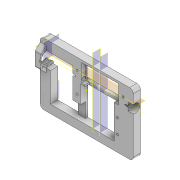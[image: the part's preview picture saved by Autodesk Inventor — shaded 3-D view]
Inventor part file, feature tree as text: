
AUTODESK INVENTOR PART (.ipt)
format: ipt  version: 2022 (Build 260153000, 153)  size: 440,832 bytes
history: native  units: mm
features: sketch x17, extrude x16, other x12, reference x8, plane x7, projected_geometry x7, fillet x3, chamfer x1, mirror x1
ambient origin geometry x8: Origin, YZ Plane, XZ Plane, XY Plane, X Axis, Y Axis, Z Axis, Center Point
bodies: Solid1 (feature_tree)
feature tree (72):
  extrude  "Extrusion1"  Depth=10.0mm
  fillet  "Fillet1"  Radius=10.0mm
  extrude  "Extrusion2"  Depth=51.0mm
  extrude  "Extrusion3"  Depth=20.0mm
  plane  "Work Plane1"
  plane  "Work Plane2"
  chamfer  "Chamfer1"  [1 undecoded]
  plane  "Work Plane3"
  extrude  "Extrusion12"  Depth=10.0mm
  extrude  "Extrusion13"  Depth=12.0mm
  mirror  "Mirror1"
  plane  "Work Plane4"
  plane  "Work Plane5"
  plane  "Arbeitsebene7"
  extrude  "Extrusion27"  Depth=7.0mm
  extrude  "Extrusion28"  Depth=0.5mm TaperAngle=0.0deg
  extrude  "Extrusion29"  Depth=0.5mm
  fillet  "Rundung6"  Radius=1.0mm
  extrude  "Extrusion37"  TaperAngle=45.0deg  [1 undecoded]
  extrude  "Extrusion38"  Depth=10.0mm
  fillet  "Rundung7"  [1 undecoded]
  extrude  "Extrusion39"  Depth=10.0mm TaperAngle=0.0deg
  other  "Arbeitsachse1"
  sketch  "Skizze44"  dims[d145=8.0mm d146=0.0mm d147=0.5mm d148=1.0mm d149=0.0mm]
  extrude  "Extrusion41"  TaperAngle=0.0deg  [1 undecoded]
  extrude  "Extrusion42"  Depth=2.0mm TaperAngle=0.0deg
  extrude  "Extrusion43"  Depth=2.5mm
  extrude  "Extrusion44"  Depth=0.5mm
  sketch  "Skizze49"  dims[d195=20.0mm d196=2.0mm d197=0.0mm d199=14.0mm d201=0.5mm d203=0.5mm d204=1.0mm d205=3.0mm d206=2.8mm d207=2.8mm d208=2.8mm d209=2.8mm d210=2.8mm d211=0.0mm d212=0.0mm d213=3.0mm d214=0.0mm d215=6.0mm d216=2.0mm d217=3.0mm d218=0.0mm d219=2.5mm d220=0.0mm]
  plane  "Arbeitsebene10"
  extrude  "Extrusion45"  Depth=0.5mm
  sketch  "Sketch1"  dims[d0=127.8mm d1=85.5mm d2=10.0mm d3=0.0mm]
  sketch  "Sketch2"  dims[d4=4.0mm d5=51.0mm]
  projected_geometry  "Projected Loop1"
  sketch  "Sketch3"  dims[d6=25.0mm d7=20.0mm]
  projected_geometry  "Projected Loop2"
  sketch  "Sketch12"  dims[d8=13.0mm]
  reference  "Reference4"
  sketch  "Sketch13"  dims[d9=6.0mm]
  sketch  "Skizze28"  dims[d10=0.0mm]
  sketch  "Skizze29"  dims[d11=1.5mm d12=0.0mm d13=0.0mm]
  reference  "Referenz13"
  sketch  "Skizze30"  dims[d14=4.0mm d15=2.0mm d16=45.0deg d38=10.0mm]
  reference  "Referenz14"
  sketch  "Skizze40"  dims[d61=30.0mm d62=-0.523599mm d63=12.0mm]
  projected_geometry  "Projizierte Kontur18"
  sketch  "Skizze41"  dims[d64=7.0mm d65=0.0mm d100=7.0mm]
  projected_geometry  "Projizierte Kontur19"
  sketch  "Skizze42"  dims[d142=0.5mm d143=40.0mm d144=0.0mm]
  reference  "Referenz22"
  reference  "Referenz23"
  reference  "Referenz24"
  reference  "Referenz25"
  sketch  "Skizze45"  dims[d150=2.0mm d151=45.0deg]
  sketch  "Skizze46"  dims[d152=45.0deg d178=10.0mm d179=0.0mm d180=0.0mm]
  projected_geometry  "Projizierte Kontur20"
  sketch  "Skizze47"  dims[d181=14.0mm d182=10.0mm d183=0.0mm]
  projected_geometry  "Projizierte Kontur21"
  sketch  "Skizze48"  dims[d184=5.0mm d187=0.0mm d188=0.0mm]
  projected_geometry  "Projizierte Kontur22"
  reference  "Referenz29"
  other  "<userpath>\Documents\GitHub\Guinardia\INVENTOR\Assembly_Guinardia_V1.iam"
  other  "Assembly_Guinardia_V1.iam"
  other  "00_PipetteTip200ul-1:2"
  other  "00_NEMA8:1"
  other  "Assembly_Guinardia_V2.iam"
  other  "Assemlby_Scanner_v1:1"
  other  "30_Scanlens_Laseradaper_v1:1"
  other  "30_Scanlens_Laseradaper_lid_v1:1"
  other  "00_Coverglass_50x24mm:2"
  other  "<userpath>\Documents\Inventor\Guinardia\INVENTOR\Assembly_Guinardia_V0.iam"
  other  "Assembly_Guinardia_V0.iam"
note: 4 required parameter values undecoded (feature->parameter linkage not recoverable at this tier; creation-order binding heuristic only, values carry confidence <= 0.55)
